# Revit family: LZR
name_source: partatom
category: Lighting Fixtures
revit_build: Autodesk Revit 2014 (Build: 20130308_1515(x64)
units: mm (PartAtom-declared; Revit-internal decimal feet)

## types (2) — shared parameters
Certification = UL 924 Listed
NFPA 101 Life Safety Code
CEC T20 Compliant
Default Elevation = 48.000"
Description = Architectural/commerical design. High performance MR-16 halogen lamps standard.
Finish = Hubbell - White
Glass = Hubbell - light Glass
Holder Material = Hubbell - Steel
LED = Hubbell - White
Lamp = Halogen / 3 Watt LED Lamp
Lens = Hubbell - Green Glass
Load Classification = Lighting
Manufacturer = DUAL-LITE
Model = LZR
Product Documentation Link = https://hubbellcdn.com
Product Page URL = https://www.hubbell.com
Type Comments = Emergency & Exit Lighting
URL = https://www.hubbell.com
Wall Plate Material = Hubbell - Black
Warranty = https://hubbellcdn.com

## per-type parameters (varying)
| type | Apparent Load | Double Face | Single Face | Wattage Comments | Watts |
| LZR-S | 4 VA | No | Yes | 3.72 W | 4 W |
| LZR-D | 5 VA | Yes | No | 5W | 5 W |

## geometry (parser evidence)
native form markers: Blend x8, Sweep x5
no freeform markers — native parametric forms only
